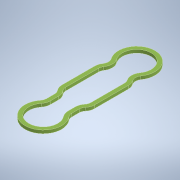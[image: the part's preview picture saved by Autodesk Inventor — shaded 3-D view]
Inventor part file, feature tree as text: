
AUTODESK INVENTOR PART (.ipt)
format: ipt  version: 2021 (Build 250183000, 183)  size: 200,704 bytes
history: native  units: mm
features: extrude x1, sketch x1
ambient origin geometry x8: Origin, YZ Plane, XZ Plane, XY Plane, X Axis, Y Axis, Z Axis, Center Point
bodies: Solid1 (feature_tree)
feature tree (2):
  extrude  "Extrusion1"  Depth=1.5mm
  sketch  "Sketch1"  dims[d0=1.0mm d1=1.0mm d2=3.0mm d3=2.6mm d4=8.3mm d5=1.0mm d6=0.4mm d7=0.4mm d8=0.4mm d9=0.4mm d10=0.4mm d11=0.4mm d12=0.4mm d13=0.4mm d14=0.4mm d15=0.4mm d16=0.4mm d17=0.4mm d18=0.4mm d19=0.4mm d20=0.4mm d21=1.5mm d22=0.0mm]
